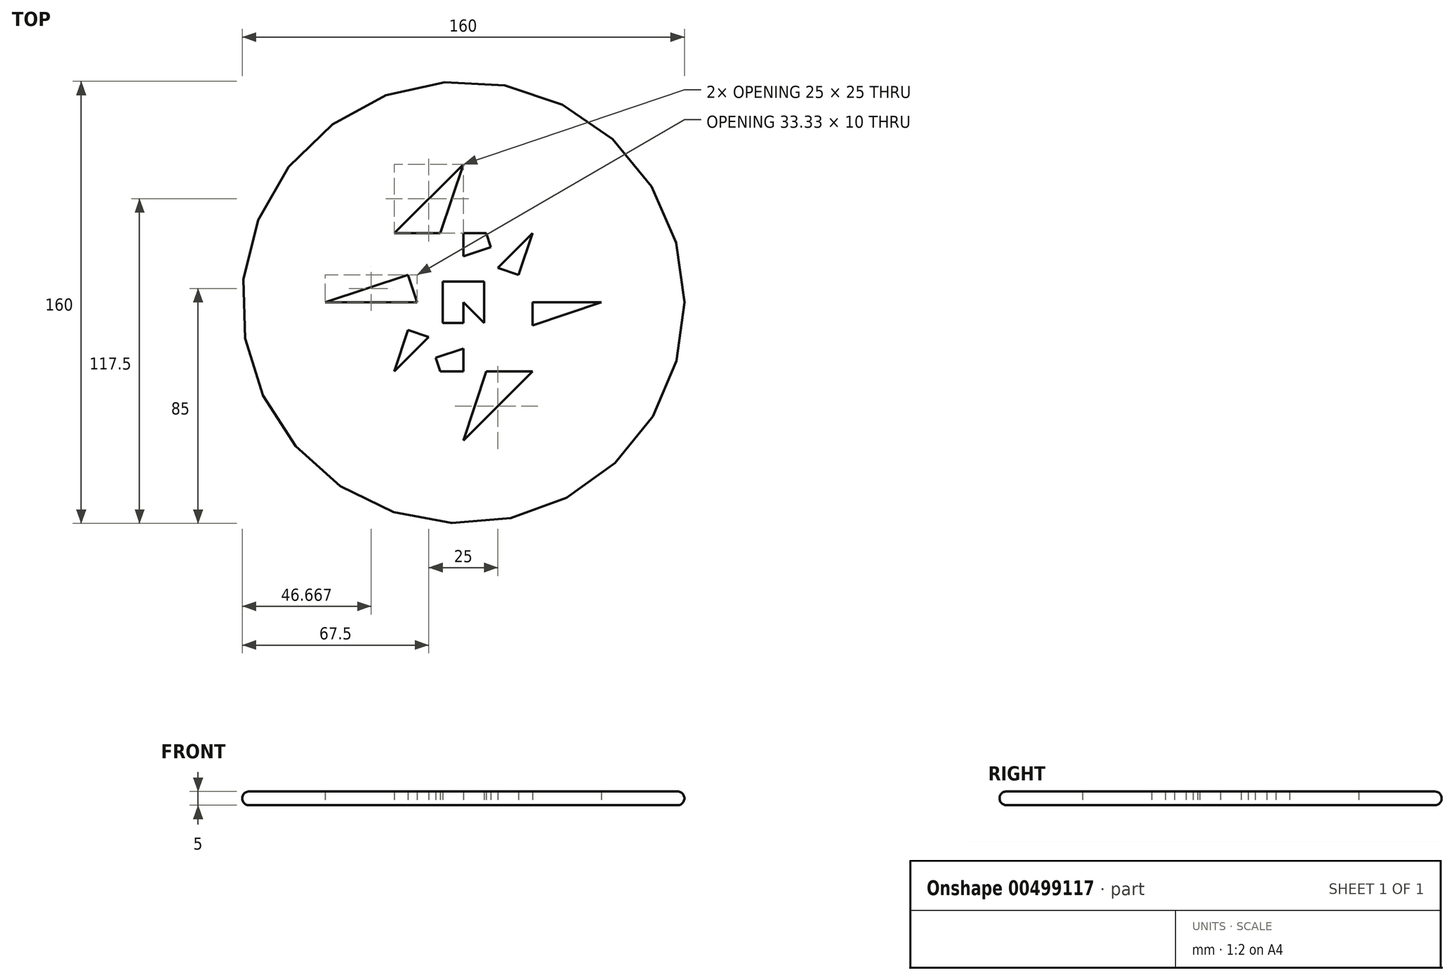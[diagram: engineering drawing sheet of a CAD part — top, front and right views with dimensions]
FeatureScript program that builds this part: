
annotation { "Feature Type Name" : "Feature", "Feature Type Description" : "" }
export const myFeature = defineFeature(function(context is Context, id is Id, definition is map)
    precondition{}
    {
        {
            var Q0;
            Q0=qCreatedBy(makeId("Top.planeOp"),FACE);
            var sketch = newSketch(context, id + "F0", { "sketchPlane" : qUnion([Q0])});
            skCircle(sketch, "E0", {"center": v(0, 0) * mm, "radius": 80 * mm});
            skSolve(sketch);
        }
        {
            var Q0;
            Q0=makeQuery(id+"F0.imprint","IMPRINT",FACE,{"disambiguationData":[TD([[makeQuery(id+"F0.imprint","IMPRINT",EDGE,{"derivedFrom":sQuery(id+"F0.wireOp",EDGE,"E0")}),1.0]])]});
            extrude(context, id + "F1", {"entities" : qUnion([Q0]), "depth" : 5 * mm});
        }
        {
            var Q0;
            Q0=qCreatedBy(makeId("Top.planeOp"),FACE);
            var sketch = newSketch(context, id + "F2", { "sketchPlane" : qUnion([Q0])});
            skLineSegment(sketch, "E1", {"start": v(0, 0) * mm, "end": v(-50, 0) * mm});
            skLineSegment(sketch, "E2", {"start": v(0, 0) * mm, "end": v(50, 0) * mm});
            skLineSegment(sketch, "E3", {"start": v(0, 0) * mm, "end": v(0, -50) * mm});
            skLineSegment(sketch, "E4", {"start": v(0, 0) * mm, "end": v(0, 50) * mm});
            skLineSegment(sketch, "E5", {"start": v(-50, 0) * mm, "end": v(0, -50) * mm});
            skLineSegment(sketch, "E6", {"start": v(0, -50) * mm, "end": v(50, 0) * mm});
            skLineSegment(sketch, "E7", {"start": v(0, 50) * mm, "end": v(50, 0) * mm});
            skLineSegment(sketch, "E8", {"start": v(0, 50) * mm, "end": v(-50, 0) * mm});
            skLineSegment(sketch, "E9", {"start": v(-50, 0) * mm, "end": v(25, -25) * mm});
            skLineSegment(sketch, "E10", {"start": v(25, -25) * mm, "end": v(-25, 25) * mm});
            skLineSegment(sketch, "E11", {"start": v(-25, 25) * mm, "end": v(25, 25) * mm});
            skLineSegment(sketch, "E12", {"start": v(25, 25) * mm, "end": v(-25, -25) * mm});
            skLineSegment(sketch, "E13", {"start": v(-25, -25) * mm, "end": v(25, -25) * mm});
            skLineSegment(sketch, "E14", {"start": v(25, -25) * mm, "end": v(25, 25) * mm});
            skLineSegment(sketch, "E15", {"start": v(-50, 0) * mm, "end": v(25, 25) * mm});
            skLineSegment(sketch, "E16", {"start": v(0, 50) * mm, "end": v(-25, -25) * mm});
            skLineSegment(sketch, "E17", {"start": v(0, 50) * mm, "end": v(25, -25) * mm});
            skLineSegment(sketch, "E18", {"start": v(50, 0) * mm, "end": v(-25, -25) * mm});
            skLineSegment(sketch, "E19", {"start": v(50, 0) * mm, "end": v(-25, 25) * mm});
            skLineSegment(sketch, "E20", {"start": v(0, -50) * mm, "end": v(-25, 25) * mm});
            skLineSegment(sketch, "E21", {"start": v(0, -50) * mm, "end": v(25, 25) * mm});
            skLineSegment(sketch, "E22.bottom", {"start": v(-7.5, -7.5) * mm, "end": v(7.5, -7.5) * mm});
            skLineSegment(sketch, "E22.top", {"start": v(-7.5, 7.5) * mm, "end": v(7.5, 7.5) * mm});
            skLineSegment(sketch, "E22.left", {"start": v(-7.5, -7.5) * mm, "end": v(-7.5, 7.5) * mm});
            skLineSegment(sketch, "E22.right", {"start": v(7.5, -7.5) * mm, "end": v(7.5, 7.5) * mm});
            skPoint(sketch, "E22.middle", {"position": v(0, 0) * mm});
            skSolve(sketch);
        }
        {
            var Q0;
            {var subQ0=sQuery(id+"F2.wireOp",EDGE,"E16");var subQ3=sQuery(id+"F2.wireOp",EDGE,"E11");var subQ5=makeQuery(id+"F2.imprint","INTERSECT",VERTEX,{"derivedFrom":[subQ3,subQ0]});Q0=makeQuery(id+"F2.imprint","IMPRINT",FACE,{"disambiguationData":[TD([[makeQuery(id+"F2.imprint","IMPRINT",EDGE,{"disambiguationData":[TD([[subQ5,1.0]])],"derivedFrom":subQ3}),1.0]])]});}
            var Q1;
            {var subQ0=sQuery(id+"F2.wireOp",EDGE,"E15");var subQ3=sQuery(id+"F2.wireOp",EDGE,"E20");var subQ5=makeQuery(id+"F2.imprint","INTERSECT",VERTEX,{"derivedFrom":[subQ0,subQ3]});Q1=makeQuery(id+"F2.imprint","IMPRINT",FACE,{"disambiguationData":[TD([[makeQuery(id+"F2.imprint","IMPRINT",EDGE,{"disambiguationData":[TD([[subQ5,1.0]])],"derivedFrom":subQ3}),1.0]])]});}
            var Q2;
            {var subQ0=sQuery(id+"F2.wireOp",EDGE,"E16");var subQ1=sQuery(id+"F2.wireOp",EDGE,"E9");var subQ2=makeQuery(id+"F2.imprint","INTERSECT",VERTEX,{"derivedFrom":[subQ1,subQ0]});Q2=makeQuery(id+"F2.imprint","IMPRINT",FACE,{"disambiguationData":[TD([[makeQuery(id+"F2.imprint","IMPRINT",EDGE,{"disambiguationData":[TD([[subQ2,-1.0]])],"derivedFrom":subQ1}),-1.0]])]});}
            var Q3;
            {var subQ0=sQuery(id+"F2.wireOp",EDGE,"E13");var subQ1=sQuery(id+"F2.wireOp",EDGE,"E3");var subQ2=makeQuery(id+"F2.imprint","INTERSECT",VERTEX,{"derivedFrom":[subQ1,subQ0]});Q3=makeQuery(id+"F2.imprint","IMPRINT",FACE,{"disambiguationData":[TD([[makeQuery(id+"F2.imprint","IMPRINT",EDGE,{"disambiguationData":[TD([[subQ2,1.0]])],"derivedFrom":subQ0}),1.0]])]});}
            var Q4;
            {var subQ0=sQuery(id+"F2.wireOp",EDGE,"E21");var subQ3=sQuery(id+"F2.wireOp",EDGE,"E13");var subQ5=makeQuery(id+"F2.imprint","INTERSECT",VERTEX,{"derivedFrom":[subQ3,subQ0]});Q4=makeQuery(id+"F2.imprint","IMPRINT",FACE,{"disambiguationData":[TD([[makeQuery(id+"F2.imprint","IMPRINT",EDGE,{"disambiguationData":[TD([[subQ5,1.0]])],"derivedFrom":subQ0}),-1.0]])]});}
            var Q5;
            {var subQ0=sQuery(id+"F2.wireOp",EDGE,"E11");var subQ1=sQuery(id+"F2.wireOp",EDGE,"E4");var subQ2=makeQuery(id+"F2.imprint","INTERSECT",VERTEX,{"derivedFrom":[subQ1,subQ0]});Q5=makeQuery(id+"F2.imprint","IMPRINT",FACE,{"disambiguationData":[TD([[makeQuery(id+"F2.imprint","IMPRINT",EDGE,{"disambiguationData":[TD([[subQ2,-1.0]])],"derivedFrom":subQ0}),-1.0]])]});}
            var Q6;
            {var subQ0=sQuery(id+"F2.wireOp",EDGE,"E21");var subQ3=sQuery(id+"F2.wireOp",EDGE,"E19");var subQ5=makeQuery(id+"F2.imprint","INTERSECT",VERTEX,{"derivedFrom":[subQ3,subQ0]});Q6=makeQuery(id+"F2.imprint","IMPRINT",FACE,{"disambiguationData":[TD([[makeQuery(id+"F2.imprint","IMPRINT",EDGE,{"disambiguationData":[TD([[subQ5,-1.0]])],"derivedFrom":subQ3}),-1.0]])]});}
            var Q7;
            {var subQ1=sQuery(id+"F2.wireOp",EDGE,"E2");var subQ3=sQuery(id+"F2.wireOp",EDGE,"E14");var subQ4=makeQuery(id+"F2.imprint","INTERSECT",VERTEX,{"derivedFrom":[subQ1,subQ3]});Q7=makeQuery(id+"F2.imprint","IMPRINT",FACE,{"disambiguationData":[TD([[makeQuery(id+"F2.imprint","IMPRINT",EDGE,{"disambiguationData":[TD([[subQ4,1.0]])],"derivedFrom":subQ3}),-1.0]])]});}
            extrude(context, id + "F3", {"entities" : qUnion([Q0, Q1, Q2, Q3, Q4, Q5, Q6, Q7]), "operationType" : NewBodyOperationType.REMOVE, "depth" : 10 * mm});
        }
        {
            var Q0;
            Q0=makeQuery(id+"F1.opExtrude","CAP_EDGE",EDGE,{"disambiguationData":[OSD([sQuery(id+"F0.wireOp",EDGE,"E0")])],"isStart":true});
            var Q1;
            Q1=makeQuery(id+"F1.opExtrude","CAP_EDGE",EDGE,{"disambiguationData":[OSD([sQuery(id+"F0.wireOp",EDGE,"E0")])],"isStart":false});
            fillet(context, id + "F4", {"entities" : qUnion([Q0, Q1]), "radius" : 2.5 * mm, "tangentPropagation" : true, "allowEdgeOverflow" : false});
        }
        {
            var Q0;
            {var subQ1=sQuery(id+"F2.wireOp",EDGE,"E3");var subQ3=sQuery(id+"F2.wireOp",EDGE,"E22.bottom");var subQ4=makeQuery(id+"F2.imprint","INTERSECT",VERTEX,{"derivedFrom":[subQ1,subQ3]});Q0=makeQuery(id+"F2.imprint","IMPRINT",FACE,{"disambiguationData":[TD([[makeQuery(id+"F2.imprint","IMPRINT",EDGE,{"disambiguationData":[TD([[subQ4,1.0]])],"derivedFrom":subQ3}),1.0]])]});}
            var Q1;
            {var subQ1=sQuery(id+"F2.wireOp",EDGE,"E1");var subQ3=sQuery(id+"F2.wireOp",EDGE,"E22.left");var subQ4=makeQuery(id+"F2.imprint","INTERSECT",VERTEX,{"derivedFrom":[subQ1,subQ3]});Q1=makeQuery(id+"F2.imprint","IMPRINT",FACE,{"disambiguationData":[TD([[makeQuery(id+"F2.imprint","IMPRINT",EDGE,{"disambiguationData":[TD([[subQ4,1.0]])],"derivedFrom":subQ3}),-1.0]])]});}
            var Q2;
            {var subQ1=sQuery(id+"F2.wireOp",EDGE,"E1");var subQ3=sQuery(id+"F2.wireOp",EDGE,"E22.left");var subQ4=makeQuery(id+"F2.imprint","INTERSECT",VERTEX,{"derivedFrom":[subQ1,subQ3]});Q2=makeQuery(id+"F2.imprint","IMPRINT",FACE,{"disambiguationData":[TD([[makeQuery(id+"F2.imprint","IMPRINT",EDGE,{"disambiguationData":[TD([[subQ4,-1.0]])],"derivedFrom":subQ3}),-1.0]])]});}
            var Q3;
            {var subQ1=sQuery(id+"F2.wireOp",EDGE,"E4");var subQ3=sQuery(id+"F2.wireOp",EDGE,"E22.top");var subQ4=makeQuery(id+"F2.imprint","INTERSECT",VERTEX,{"derivedFrom":[subQ1,subQ3]});Q3=makeQuery(id+"F2.imprint","IMPRINT",FACE,{"disambiguationData":[TD([[makeQuery(id+"F2.imprint","IMPRINT",EDGE,{"disambiguationData":[TD([[subQ4,1.0]])],"derivedFrom":subQ3}),-1.0]])]});}
            var Q4;
            {var subQ1=sQuery(id+"F2.wireOp",EDGE,"E4");var subQ3=sQuery(id+"F2.wireOp",EDGE,"E22.top");var subQ4=makeQuery(id+"F2.imprint","INTERSECT",VERTEX,{"derivedFrom":[subQ1,subQ3]});Q4=makeQuery(id+"F2.imprint","IMPRINT",FACE,{"disambiguationData":[TD([[makeQuery(id+"F2.imprint","IMPRINT",EDGE,{"disambiguationData":[TD([[subQ4,-1.0]])],"derivedFrom":subQ3}),-1.0]])]});}
            var Q5;
            {var subQ1=sQuery(id+"F2.wireOp",EDGE,"E2");var subQ3=sQuery(id+"F2.wireOp",EDGE,"E22.right");var subQ4=makeQuery(id+"F2.imprint","INTERSECT",VERTEX,{"derivedFrom":[subQ1,subQ3]});Q5=makeQuery(id+"F2.imprint","IMPRINT",FACE,{"disambiguationData":[TD([[makeQuery(id+"F2.imprint","IMPRINT",EDGE,{"disambiguationData":[TD([[subQ4,-1.0]])],"derivedFrom":subQ3}),1.0]])]});}
            var Q6;
            {var subQ1=sQuery(id+"F2.wireOp",EDGE,"E2");var subQ3=sQuery(id+"F2.wireOp",EDGE,"E22.right");var subQ4=makeQuery(id+"F2.imprint","INTERSECT",VERTEX,{"derivedFrom":[subQ1,subQ3]});Q6=makeQuery(id+"F2.imprint","IMPRINT",FACE,{"disambiguationData":[TD([[makeQuery(id+"F2.imprint","IMPRINT",EDGE,{"disambiguationData":[TD([[subQ4,1.0]])],"derivedFrom":subQ3}),1.0]])]});}
            extrude(context, id + "F5", {"entities" : qUnion([Q0, Q1, Q2, Q3, Q4, Q5, Q6]), "operationType" : NewBodyOperationType.REMOVE, "depth" : 25 * mm});
        }
    });
